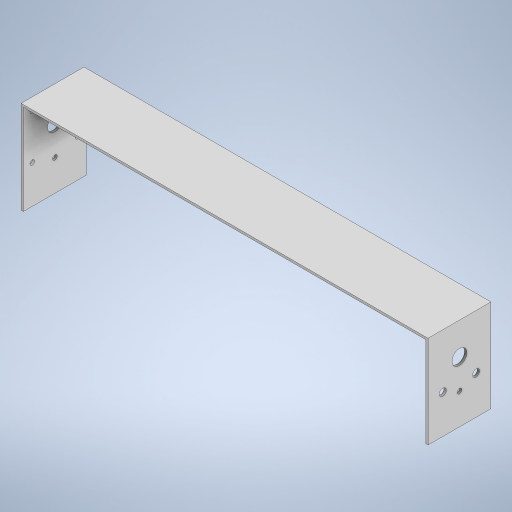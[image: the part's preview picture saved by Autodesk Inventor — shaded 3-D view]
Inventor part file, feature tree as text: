
AUTODESK INVENTOR PART (.ipt)
format: ipt  version: 2024 (Build 280153000, 153)  size: 263,680 bytes
history: native  units: in
note: dims shown in document units (in); Inventor stores cm internally (conversion verified against a paired STEP export)
features: extrude x5, sketch x5
ambient origin geometry x8: Origin, YZ Plane, XZ Plane, XY Plane, X Axis, Y Axis, Z Axis, Center Point
bodies: Solid1 (feature_tree)
feature tree (10):
  extrude  "Extrusion1"  Depth=2.5in
  extrude  "Extrusion2"  Depth=0.0625in
  extrude  "Extrusion3"  Depth=0.0625in
  extrude  "Extrusion4"  Depth=0.3976in
  extrude  "Extrusion5"  TaperAngle=0.0deg  [1 undecoded]
  sketch  "Sketch1"  dims[d0=11.0in d1=2.5in]
  sketch  "Sketch2"  dims[d2=1.7in d3=0.0in d4=0.0625in]
  sketch  "Sketch3"  dims[d5=0.0625in d6=0.0625in]
  sketch  "Sketch4"  dims[d7=1.5in d8=0.0in d9=0.3976in]
  sketch  "Sketch5"  dims[d10=0.8in d11=0.0in d12=0.0in d13=0.125in d15=0.8in d16=0.4in d17=0.6in d18=0.1875in d19=1.0in d20=0.0in d21=0.125in d22=0.6102in d23=0.6102in d24=1.0in d25=0.0in]
note: 1 required parameter value undecoded (feature->parameter linkage not recoverable at this tier; creation-order binding heuristic only, values carry confidence <= 0.55)
